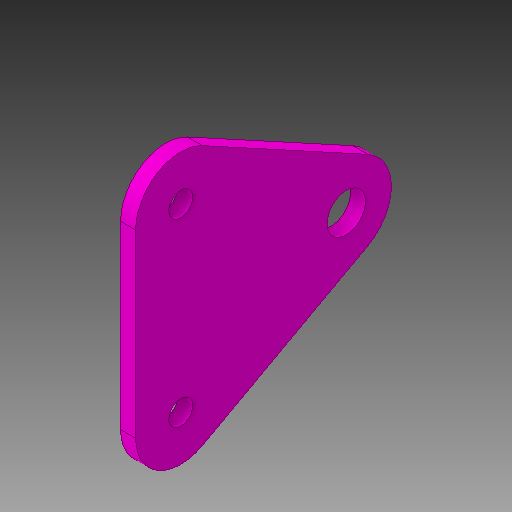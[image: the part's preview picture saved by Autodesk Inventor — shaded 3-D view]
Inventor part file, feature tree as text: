
AUTODESK INVENTOR PART (.ipt)
format: ipt  version: 2017 SP1 (Build 210196100, 196)  size: 111,616 bytes
history: native  units: in
note: dims shown in document units (in); Inventor stores cm internally (conversion verified against a paired STEP export)
features: extrude x1, sketch x1
ambient origin geometry x8: Origin, YZ Plane, XZ Plane, XY Plane, X Axis, Y Axis, Z Axis, Center Point
bodies: Solid1 (feature_tree)
feature tree (2):
  extrude  "Extrusion1"  Depth=0.125in
  sketch  "Sketch1"  dims[d0=0.2in d2=1.5in d3=0.32in d4=1.375in d5=0.375in d6=0.125in d7=0.0in]
